FCSTD DOCUMENT  (FreeCAD 0.20R29603 (Git))
Label: thesis cart wheel plate
License: All rights reserved
LicenseURL: http://en.wikipedia.org/wiki/All_rights_reserved
objects: Sketcher::SketchObject×1, PartDesign::Body×1
note: 2 computed .brp shape members not serialized (recipe doc carries the construction recipe); baked Part::Feature solids carry a one-line shape summary decoded from their .brp

FEATURE [Sketcher::SketchObject] Sketch
  FullyConstrained = true
  MapMode = 5
  Support = -> [XY_Plane]
  sketch-geometry (30):
    g0: LineSegment StartX=-27.5 StartY=0 StartZ=0 EndX=27.5 EndY=0 EndZ=0
    g1: Circle CenterX=-27.5 CenterY=0 CenterZ=0 NormalX=0 NormalY=0 NormalZ=1 AngleXU=0 Radius=3.5
    g2: Circle CenterX=27.5 CenterY=0 CenterZ=0 NormalX=0 NormalY=0 NormalZ=1 AngleXU=0 Radius=3.5
    g3: Circle CenterX=12.5 CenterY=0 CenterZ=0 NormalX=0 NormalY=0 NormalZ=1 AngleXU=0 Radius=0.85
    g4: Circle CenterX=-12.5 CenterY=0 CenterZ=0 NormalX=0 NormalY=0 NormalZ=1 AngleXU=0 Radius=0.85
    g5: Circle CenterX=-22.5 CenterY=9 CenterZ=0 NormalX=0 NormalY=0 NormalZ=1 AngleXU=0 Radius=0.85
    g6: Circle CenterX=22.5 CenterY=9 CenterZ=0 NormalX=0 NormalY=0 NormalZ=1 AngleXU=0 Radius=0.85
    g7: Circle CenterX=12.5 CenterY=17 CenterZ=0 NormalX=0 NormalY=0 NormalZ=1 AngleXU=0 Radius=0.85
    g8: Circle CenterX=-12.5 CenterY=17 CenterZ=0 NormalX=0 NormalY=0 NormalZ=1 AngleXU=0 Radius=0.85
    g9: LineSegment StartX=-12.5 StartY=-20 StartZ=0 EndX=-12.5 EndY=20 EndZ=0
    g10: LineSegment StartX=-10.7461 StartY=20 StartZ=0 EndX=10.7461 EndY=20 EndZ=0
    g11: LineSegment StartX=12.5 StartY=20 StartZ=0 EndX=12.5 EndY=-20 EndZ=0
    g12: LineSegment StartX=10.7461 StartY=-20 StartZ=0 EndX=-10.7461 EndY=-20 EndZ=0
    g13: GeomPoint X=0 Y=0 Z=0
    g14: LineSegment StartX=-13.8696 StartY=-18.9043 StartZ=0 EndX=-31.6435 EndY=-4.68521 EndZ=0
    g15: LineSegment StartX=-31.6435 StartY=4.68521 StartZ=0 EndX=-13.8696 EndY=18.9043 EndZ=0
    g16: LineSegment StartX=13.8696 StartY=18.9043 StartZ=0 EndX=31.6435 EndY=4.68521 EndZ=0
    g17: LineSegment StartX=13.8696 StartY=-18.9043 StartZ=0 EndX=31.6435 EndY=-4.68521 EndZ=0
    g18: ArcOfCircle CenterX=-10.7461 CenterY=15 CenterZ=0 NormalX=0 NormalY=0 NormalZ=1 AngleXU=0 Radius=5 StartAngle=1.5708 EndAngle=2.24554
    g19: GeomPoint X=-12.5 Y=20 Z=0
    g20: ArcOfCircle CenterX=10.7461 CenterY=15 CenterZ=0 NormalX=0 NormalY=0 NormalZ=1 AngleXU=0 Radius=5 StartAngle=0.896055 EndAngle=1.5708
    g21: GeomPoint X=12.5 Y=20 Z=0
    g22: ArcOfCircle CenterX=27.8953 CenterY=2.3e-15 CenterZ=0 NormalX=0 NormalY=0 NormalZ=1 AngleXU=0 Radius=6 StartAngle=5.38713 EndAngle=7.17924
    g23: GeomPoint X=37.5 Y=0 Z=0
    g24: ArcOfCircle CenterX=10.7461 CenterY=-15 CenterZ=0 NormalX=0 NormalY=0 NormalZ=1 AngleXU=0 Radius=5 StartAngle=4.71239 EndAngle=5.38713
    g25: GeomPoint X=12.5 Y=-20 Z=0
    g26: ArcOfCircle CenterX=-10.7461 CenterY=-15 CenterZ=0 NormalX=0 NormalY=0 NormalZ=1 AngleXU=0 Radius=5 StartAngle=4.03765 EndAngle=4.71239
    g27: GeomPoint X=-12.5 Y=-20 Z=0
    g28: ArcOfCircle CenterX=-27.8953 CenterY=1.3e-15 CenterZ=0 NormalX=0 NormalY=0 NormalZ=1 AngleXU=0 Radius=6 StartAngle=2.24554 EndAngle=4.03765
    g29: GeomPoint X=-37.5 Y=0 Z=0
  constraints (72):
    c: Horizontal(g0)
    c: DistanceX(g0,g0) = 55
    c: PointOnObject(g0,g-1)
    c: DistanceX(g0,g-1) = 27.5
    c: Coincident(g1,g0)
    c: Coincident(g2,g0)
    c: Equal(g1,g2)
    c: Diameter(g1) = 7
    c: PointOnObject(g3,g0)
    c: PointOnObject(g4,g0)
    c: DistanceX(g3,g2) = 15
    c: DistanceX(g1,g4) = 15
    c: Vertical(g8,g4)
    c: Vertical(g3,g7)
    c: Horizontal(g7,g8)
    c: Horizontal(g5,g6)
    c: DistanceX(g3,g6) = 10
    c: DistanceX(g5,g4) = 10
    c: DistanceY(g3,g7) = 17
    c: DistanceY(g3,g6) = 9
    c: Equal(g8,g7)
    c: Equal(g8,g5)
    c: Equal(g8,g4)
    c: Equal(g8,g3)
    c: Equal(g8,g6)
    c: Diameter(g8) = 1.7
    c: Coincident(g9,g19)
    c: Coincident(g21,g11)
    c: Coincident(g11,g25)
    c: Coincident(g27,g9)
    c: Horizontal(g10)
    c: Horizontal(g12)
    c: Vertical(g9)
    c: Vertical(g11)
    c: Symmetric(g21,g9,g13)
    c: Coincident(g13,g-1)
    c: Vertical(g19,g8)
    c: DistanceY(g9,g9) = 40
    c: PointOnObject(g29,g-1)
    c: PointOnObject(g23,g-1)
    c: DistanceX(g29,g1) = 10
    c: DistanceX(g2,g23) = 10
    c: PointOnObject(g19,g15)
    c: PointOnObject(g19,g10)
    c: Tangent(g15,g18) = 1.5708
    c: Tangent(g10,g18) = 1.5708
    c: PointOnObject(g21,g10)
    c: PointOnObject(g21,g16)
    c: Tangent(g10,g20) = 1.5708
    c: Tangent(g16,g20) = 1.5708
    c: PointOnObject(g23,g16)
    c: PointOnObject(g23,g17)
    c: Tangent(g16,g22) = 1.5708
    c: Tangent(g17,g22) = -1.5708
    c: PointOnObject(g25,g17)
    c: PointOnObject(g25,g12)
    c: Tangent(g17,g24) = -1.5708
    c: Tangent(g12,g24) = 1.5708
    c: PointOnObject(g27,g12)
    c: PointOnObject(g27,g14)
    c: Tangent(g12,g26) = 1.5708
    c: Tangent(g14,g26) = 1.5708
    c: PointOnObject(g29,g14)
    c: PointOnObject(g29,g15)
    c: Tangent(g14,g28) = 1.5708
    c: Tangent(g15,g28) = 1.5708
    c: Equal(g18,g20)
    c: Equal(g18,g24)
    c: Equal(g18,g26)
    c: Radius(g18) = 5
    c: Equal(g28,g22)
    c: Radius(g28) = 6
FEATURE [PartDesign::Body] Body
  Group = -> [Sketch]
  Origin = -> Origin
